# Revit family: QF_MACOM_CH73C-2T_3T
name_source: partatom
category: Equipamento especial
units: mm (PartAtom-declared; Revit-internal decimal feet)

## family parameters
Com base no plano de trabalho = Não
Compartilhado = Não
Corte com vazios quando carregada = Não
Cota do conector redondo = Utilizar diâmetro
Número OmniClass = 23.40.40.14.17.14
Ponto de cálculo do ambiente = Não
Sempre na vertical = Sim
Tipo de parte = Normal
Título OmniClass = Hot Plates

## types (2) — shared parameters
Cycle = 60 Hz
Depth = 745,000 mm
Descrição = CHAPA 700HP MACOM 1080 ELETRICO
Elec Connection Height = 87,000 mm
Electric Power = 12000 W
Elevação padrão = 0,000 mm
Fabricante = MACOM
Height = 337,000 mm
Ingress Protection Code = IP 23
URL = https://www.acosmacom.com.br
Volume = 0,20 m³
Weigth = 153,00 kg
Width = 1080,000 mm

## per-type parameters (varying)
| type | Operational Current | Volts |
| CH73C-2T | 32 A | 220 V |
| CH73C-3T | 18 A | 380 V |

note: column(s) folded — value = type name in every type: Modelo

## geometry (parser evidence)
native form markers: Sweep x1
no freeform markers — native parametric forms only
